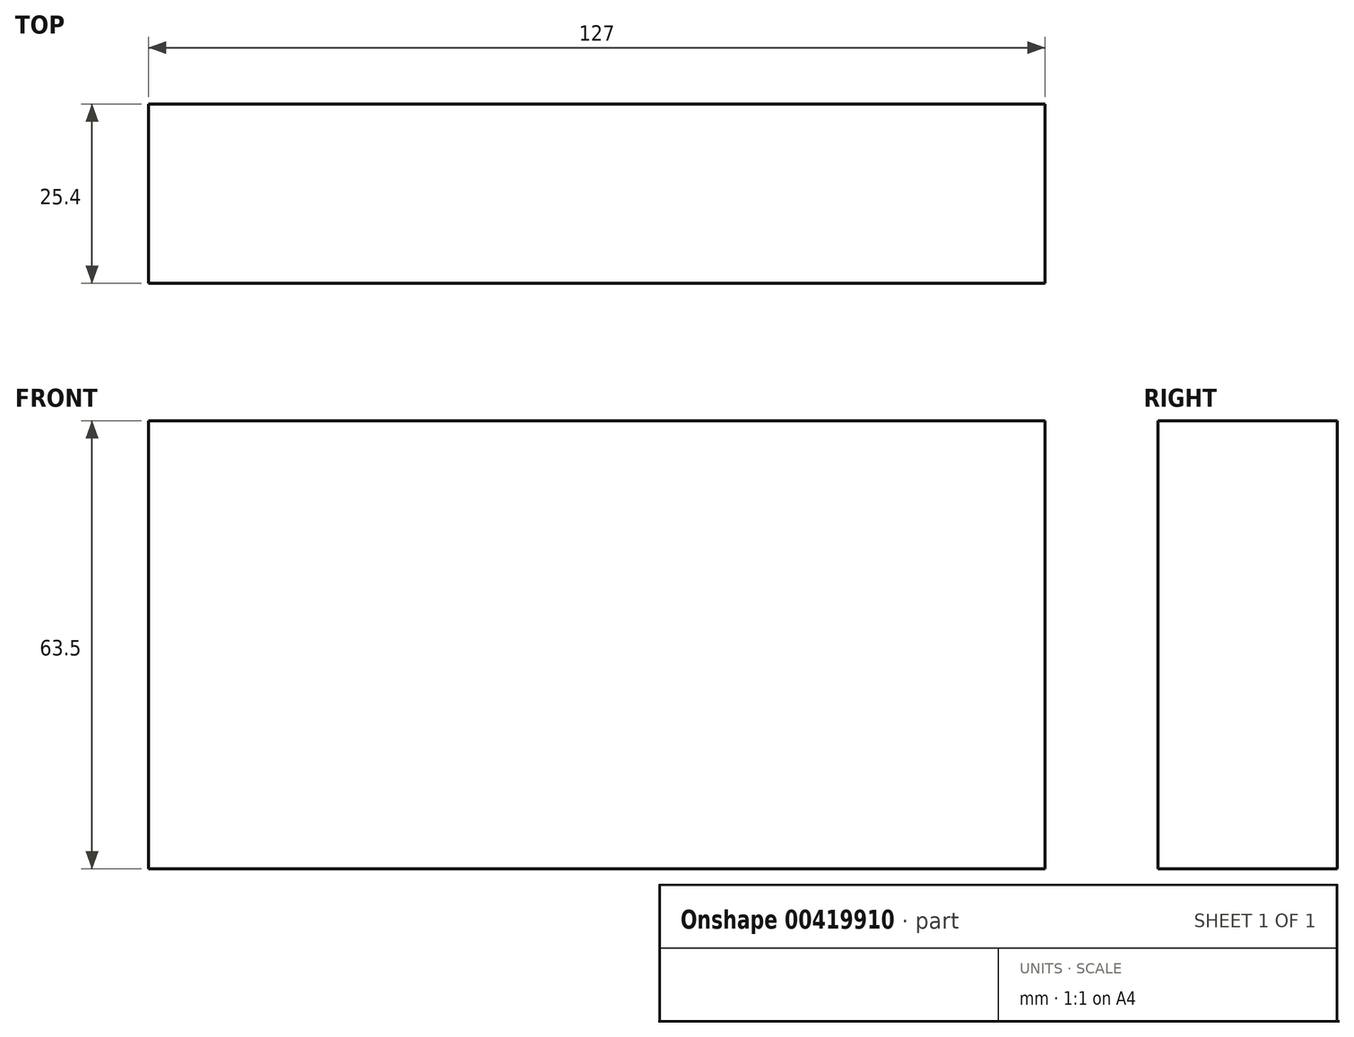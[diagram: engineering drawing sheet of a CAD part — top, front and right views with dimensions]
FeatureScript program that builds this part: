
annotation { "Feature Type Name" : "Feature", "Feature Type Description" : "" }
export const myFeature = defineFeature(function(context is Context, id is Id, definition is map)
    precondition{}
    {
        {
            var Q0;
            Q0=qCreatedBy(makeId("Top.planeOp"),FACE);
            var sketch = newSketch(context, id + "F0", { "sketchPlane" : qUnion([Q0])});
            skLineSegment(sketch, "E0.bottom", {"start": v(0, 0) * mm, "end": v(127, 0) * mm});
            skLineSegment(sketch, "E0.top", {"start": v(0, 25.4) * mm, "end": v(127, 25.4) * mm});
            skLineSegment(sketch, "E0.left", {"start": v(0, 0) * mm, "end": v(0, 25.4) * mm});
            skLineSegment(sketch, "E0.right", {"start": v(127, 0) * mm, "end": v(127, 25.4) * mm});
            skSolve(sketch);
        }
        {
            var Q0;
            Q0=makeQuery(id+"F0.imprint","IMPRINT",FACE,{"disambiguationData":[TD([[makeQuery(id+"F0.imprint","IMPRINT",EDGE,{"derivedFrom":sQuery(id+"F0.wireOp",EDGE,"E0.bottom")}),1.0]])]});
            extrude(context, id + "F1", {"entities" : qUnion([Q0]), "depth" : 63.5 * mm});
        }
    });
